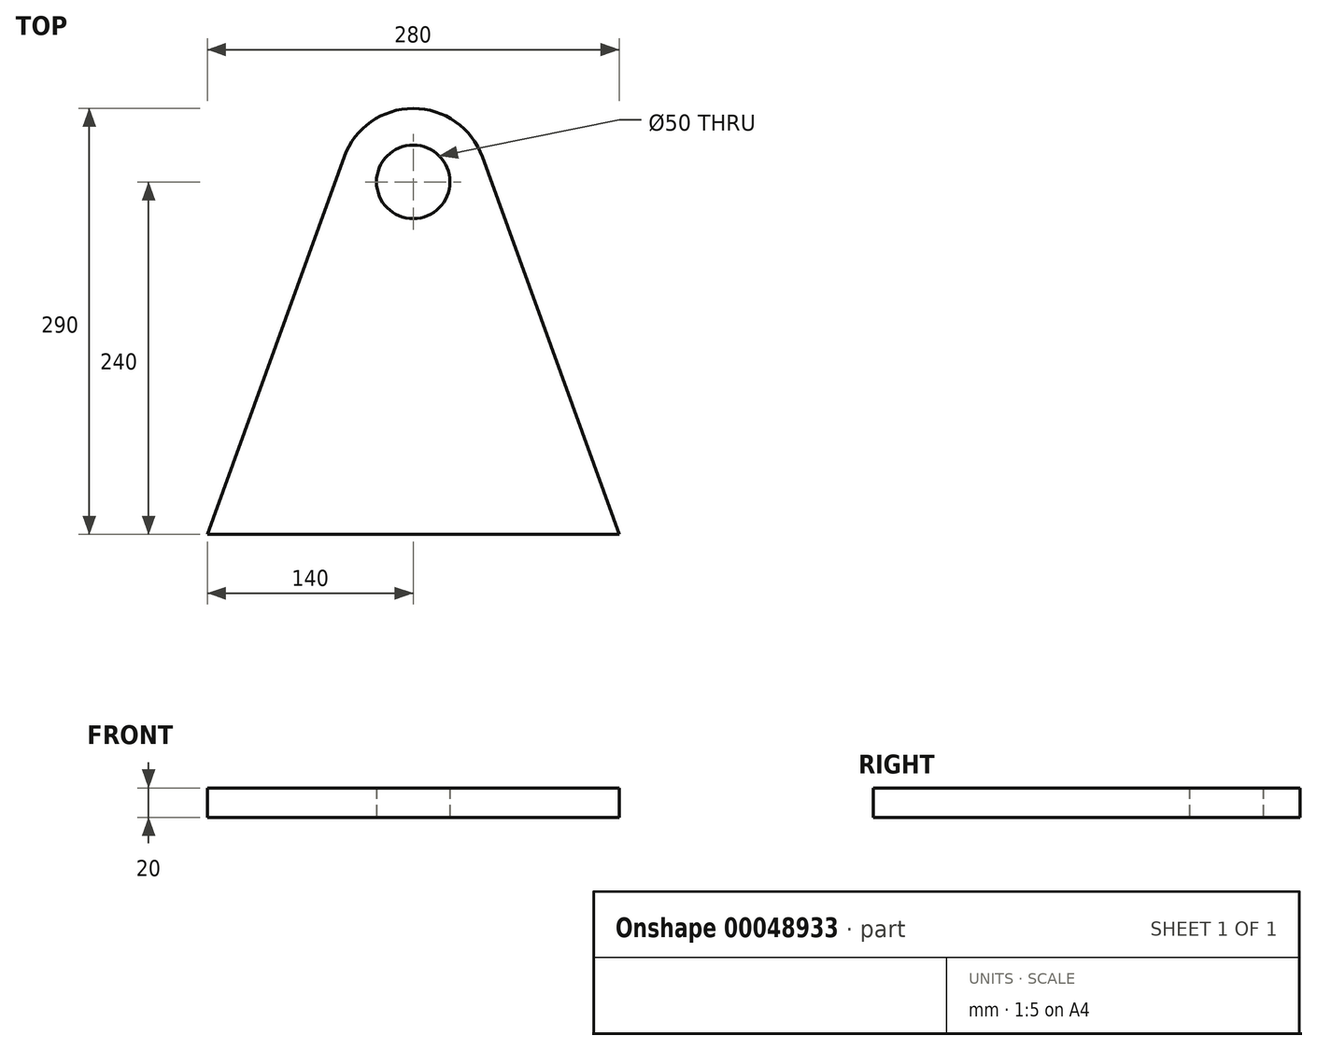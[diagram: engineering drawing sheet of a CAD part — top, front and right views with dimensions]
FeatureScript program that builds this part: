
annotation { "Feature Type Name" : "Feature", "Feature Type Description" : "" }
export const myFeature = defineFeature(function(context is Context, id is Id, definition is map)
    precondition{}
    {
        {
            var Q0;
            Q0=qCreatedBy(makeId("Top.planeOp"),FACE);
            var sketch = newSketch(context, id + "F0", { "sketchPlane" : qUnion([Q0])});
            skCircle(sketch, "E0", {"center": v(0, 0) * mm, "radius": 25 * mm});
            skCircle(sketch, "E1", {"center": v(0, 0) * mm, "radius": 50 * mm});
            skLineSegment(sketch, "E2", {"start": v(0, 0) * mm, "end": v(0, -240) * mm, "construction": true});
            skLineSegment(sketch, "E3", {"start": v(0, -240) * mm, "end": v(140, -240) * mm});
            skLineSegment(sketch, "E4", {"start": v(140, -240) * mm, "end": v(47.02, 17.01) * mm});
            skLineSegment(sketch, "E5", {"start": v(0, -240) * mm, "end": v(-140, -240) * mm});
            skLineSegment(sketch, "E6", {"start": v(-140, -240) * mm, "end": v(-47.02, 17.01) * mm});
            skSolve(sketch);
        }
        {
            var Q0;
            Q0 = qSketchRegion(id + "F0", true);
            extrude(context, id + "F1", {"entities" : qUnion([Q0]), "depth" : 20 * mm});
        }
    });
